# Revit family: CCFPRO-D2_AUA02211050001
name_source: partatom
category: Lighting Fixtures
units: mm (PartAtom-declared; Revit-internal decimal feet)

## family parameters
Cut with Voids When Loaded = No
Host = Face
Light Source = Yes
Part Type = Normal
Room Calculation Point = No
Round Connector Dimension = Use Diameter
Shared = No

## types (5) — shared parameters
Apparent Load = 3 VA
Clevertronics_AS2293 Classification = C0=D3.2 C90=B16
Clevertronics_Applicable Standards = AS/NZS3820, CISPR15, AS/NZS2293.3
Clevertronics_Battery = 3.2V 1100mAh
Clevertronics_Battery Type = Lithium Iron Phosphate
Clevertronics_Charger Method = Intelligent Current Limited Constant Voltage
Clevertronics_Construction = Fire-retardant PC/ABS Body with Polycarbonate Diffuser
Clevertronics_Diffuser = All directional inserts included in the box
Clevertronics_Height = 214 mm  [stored 0.7021 ft]
Clevertronics_IP Rating = IP20
Clevertronics_Length = 367 mm  [stored 1.20407 ft]
Clevertronics_MIC Number = AUA02211050001
Clevertronics_Material = Clevertronics_Plastic
Clevertronics_Mounting = Wall, Ceiling Single-Sided & Ceiling Double-Sided
Clevertronics_Operating Mode = Maintained
Clevertronics_Operating Temperature = 1˚C to 40˚C
Clevertronics_Operating Voltage = 240V AC; 50Hz
Clevertronics_Power Consumption = 2.8 Watts (Standby), 3.9 Watts (Max)
Clevertronics_Product Description = LP Premium Cleverfit PRO Emergency Exit, DALI-2
Clevertronics_Replacement Battery = Battery : 1550105
Clevertronics_Replacement Driver = EM Driver : 8003152
Clevertronics_Replacement Lamp = LED Strip : 8002710
Clevertronics_Testing Node = DALI-2 Note : 8003062
Clevertronics_Testing System = DALI-2
Clevertronics_Viewing Distance = 24m
Clevertronics_Weight = 2.5Kg
Clevertronics_Width = 72 mm  [stored 0.23622 ft]
Color Filter = 16777215
Default Elevation = 1200 mm
Description = LP Premium Cleverfit PRO Emergency Exit, DALI-2
Dimming Lamp Color Temperature Shift = <None>
Indication Right 'Face Two' = No
Lamp = 6 x LED, 100,000 hours
Manufacturer = Clevertronics
Model = CCFPRO-D2
Photometric Web File = ll20952 - CCFPRO-ZW (CT10622, Classification).IES
Tilt Angle = -90.00°
URL = https://clevertronics.com.au
zero-valued in all types: Clevertronics_Annotation Size

## per-type parameters (varying)
| type | Indication Left 'Face Two' | Indication Left 'Face one' | Indication Right 'Face one' | Runing Man common arrow | Straight line 'Face one' | Straight line 'Face two' |
| Runing Man Single | No | No | No | No | Yes | No |
| Running Man Common arrow | Yes | No | No | Yes | No | No |
| Runing Man Right (Single) | No | No | Yes | No | No | No |
| Runing Man Double Sided | No | No | No | No | Yes | Yes |
| Runing Man Left (Single) | No | Yes | No | No | No | No |

note: [stored X ft] marks values corroborated as IEEE doubles in the binary element streams (Revit-internal decimal feet)

## geometry (parser evidence)
native form markers: Blend x2, Sweep x3
no freeform markers — native parametric forms only
